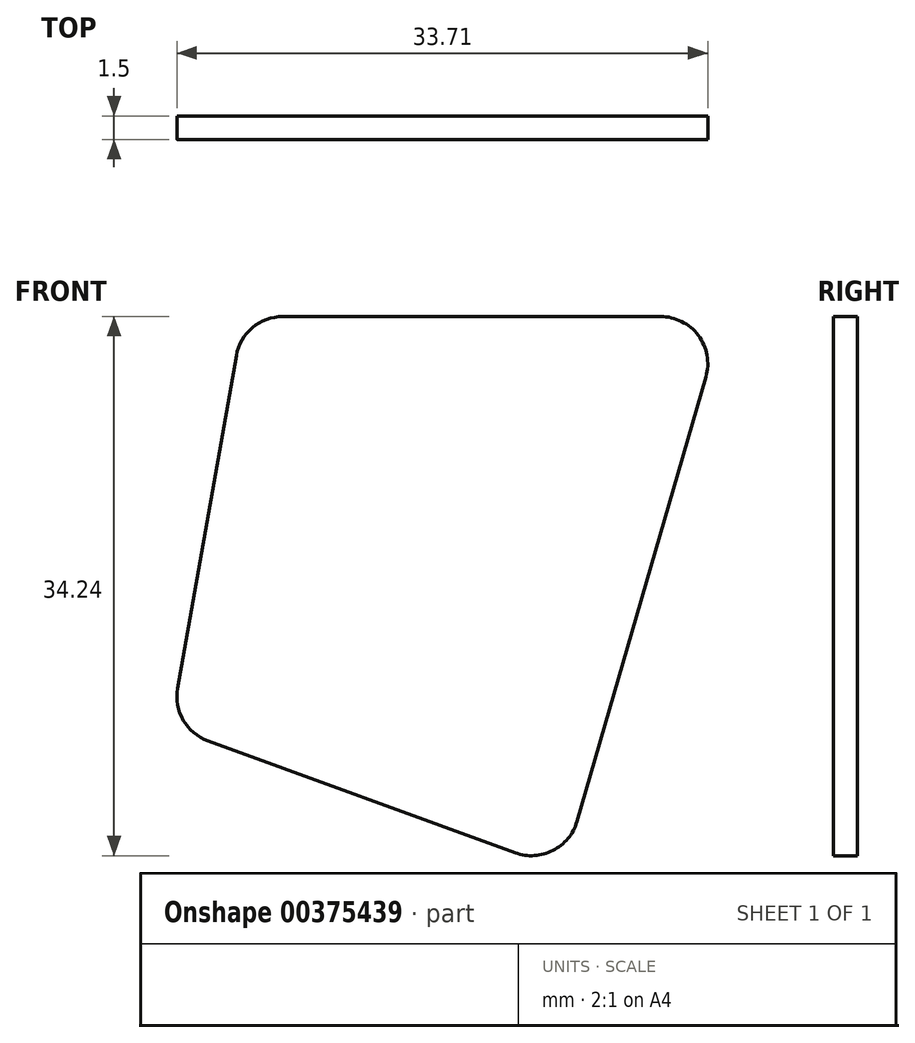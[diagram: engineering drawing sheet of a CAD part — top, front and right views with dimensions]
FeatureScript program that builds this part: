
annotation { "Feature Type Name" : "Feature", "Feature Type Description" : "" }
export const myFeature = defineFeature(function(context is Context, id is Id, definition is map)
    precondition{}
    {
        {
            var Q0;
            Q0=qCreatedBy(makeId("Front.planeOp"),FACE);
            var sketch = newSketch(context, id + "F0", { "sketchPlane" : qUnion([Q0])});
            skLineSegment(sketch, "E0", {"start": v(-47.85, 40.11) * mm, "end": v(-17.35, 40.11) * mm});
            skLineSegment(sketch, "E1", {"start": v(-17.35, 40.11) * mm, "end": v(-27.55, 4.95) * mm});
            skLineSegment(sketch, "E2", {"start": v(-27.55, 4.95) * mm, "end": v(-52.45, 14.01) * mm});
            skLineSegment(sketch, "E3", {"start": v(-52.45, 14.01) * mm, "end": v(-47.85, 40.11) * mm});
            skSolve(sketch);
        }
        {
            var Q0;
            Q0=makeQuery(id+"F0.imprint","IMPRINT",FACE,{"disambiguationData":[TD([[makeQuery(id+"F0.imprint","IMPRINT",EDGE,{"derivedFrom":sQuery(id+"F0.wireOp",EDGE,"E0")}),-1.0]])]});
            extrude(context, id + "F1", {"entities" : qUnion([Q0]), "depth" : 1.5 * mm});
        }
        {
            var Q0;
            Q0=makeQuery(id+"F1.opExtrude","SWEPT_EDGE",EDGE,{"disambiguationData":[OSD([sQuery(id+"F0.wireOp",EDGE,"E2"),sQuery(id+"F0.wireOp",EDGE,"E3")])]});
            var Q1;
            Q1=makeQuery(id+"F1.opExtrude","SWEPT_EDGE",EDGE,{"disambiguationData":[OSD([sQuery(id+"F0.wireOp",EDGE,"E0"),sQuery(id+"F0.wireOp",EDGE,"E3")])]});
            var Q2;
            Q2=makeQuery(id+"F1.opExtrude","SWEPT_EDGE",EDGE,{"disambiguationData":[OSD([sQuery(id+"F0.wireOp",EDGE,"E0"),sQuery(id+"F0.wireOp",EDGE,"E1")])]});
            var Q3;
            Q3=makeQuery(id+"F1.opExtrude","SWEPT_EDGE",EDGE,{"disambiguationData":[OSD([sQuery(id+"F0.wireOp",EDGE,"E1"),sQuery(id+"F0.wireOp",EDGE,"E2")])]});
            fillet(context, id + "F2", {"entities" : qUnion([Q0, Q1, Q2, Q3]), "radius" : 3 * mm, "tangentPropagation" : true, "allowEdgeOverflow" : false});
        }
    });
